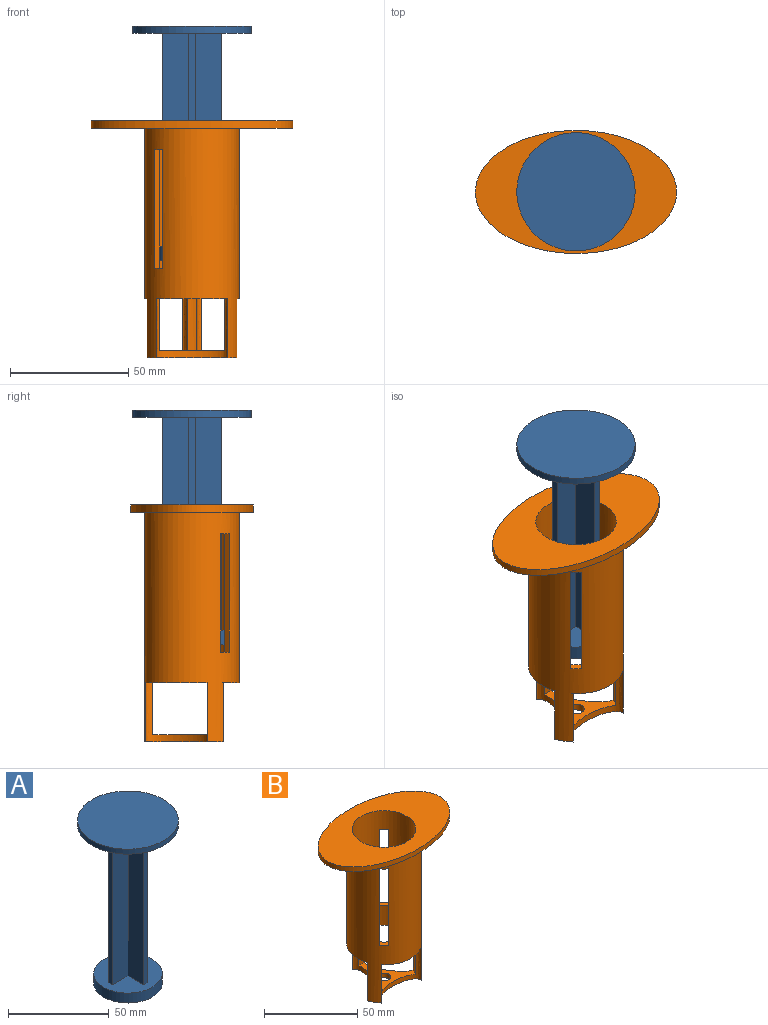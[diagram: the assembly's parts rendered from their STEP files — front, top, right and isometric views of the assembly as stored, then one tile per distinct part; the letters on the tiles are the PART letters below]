
ASSEMBLY  parts=2 mates=1
PART A: 18 faces, bbox 50x50x99 mm
  f0: plane 90x3mm, normal (0,1,0), area 270mm2, adj f1,f11,f12,f16
  f1: plane 90x11mm, normal (-1,0,0), area 990mm2, adj f0,f2,f12,f16
  f2: plane 90x11mm, normal (0,1,0), area 990mm2, adj f1,f3,f12,f16
  f3: plane 90x3mm, normal (-1,0,0), area 270mm2, adj f2,f4,f12,f16
  f4: plane 90x11mm, normal (0,-1,0), area 990mm2, adj f3,f5,f12,f16
  f5: plane 90x11mm, normal (-1,0,0), area 990mm2, adj f4,f6,f12,f16
  f6: plane 90x3mm, normal (0,-1,0), area 270mm2, adj f5,f7,f12,f16
  f7: plane 90x11mm, normal (1,0,0), area 990mm2, adj f6,f8,f12,f16
  f8: plane 90x11mm, normal (0,-1,0), area 990mm2, adj f7,f9,f12,f16
  f9: plane 90x3mm, normal (1,0,0), area 270mm2, adj f8,f10,f12,f16
  f10: plane 90x11mm, normal (0,1,0), area 990mm2, adj f9,f11,f12,f16
  f11: plane 90x11mm, normal (1,0,0), area 990mm2, adj f0,f10,f12,f16
  f12: plane 34x34mm, normal (0,0,1), area 766.9mm2, adj f0,f1,f2,f3,f4,f5,f6,f7
  f13: cylinder r=17mm len=34mm, axis (0,0,-1), area 640.9mm2, adj f12,f14
  f14: plane 34x34mm, normal (0,0,-1), area 907.9mm2, adj f13
  f15: cylinder r=25mm len=50mm, axis (0,0,1), area 471.2mm2, adj f16,f17
  f16: plane 50x50mm, normal (0,0,-1), area 1822.5mm2, adj f0,f1,f2,f3,f4,f5,f6,f7
  f17: plane 50x50mm, normal (0,0,1), area 1963.5mm2, adj f15
PART B: 22 faces, bbox 85x52x100 mm
  f0: cylinder r=20mm len=97mm, axis (0,0,-1), area 9146.2mm2, adj f2,f5,f6,f8,f9,f10,f11,f13
  f1: cylinder r=17mm len=97mm, axis (0,0,-1), area 7783.9mm2, adj f3,f4,f5,f6,f8,f9,f10,f11
  f2: plane 37.92x33.24mm, normal (0,0,-1), area 315.7mm2, adj f0,f5,f7,f8,f10
  f3: plane 85x52mm, normal (0,0,1), area 2563.5mm2, adj f1,f12
  f4: plane 31.3x27.23mm, normal (0,0,1), area 266.2mm2, adj f1,f5,f7,f8,f10
  f5: extruded ~29.98x25mm, area 258.3mm2, adj f0,f1,f2,f4,f6
  f6: plane 30x9.77mm, normal (0,0,-1), area 99.7mm2, adj f0,f1,f5
  f7: cylinder r=3.5mm len=7mm, axis (0,0,-1), area 66mm2, adj f2,f4
  f8: extruded ~26.49x25mm, area 258.3mm2, adj f0,f1,f2,f4,f9
  f9: plane 26.49x17.92mm, normal (0,0,-1), area 99.7mm2, adj f0,f1,f8
  f10: extruded ~26.49x25mm, area 258.3mm2, adj f0,f1,f2,f4,f11
  f11: plane 26.49x17.92mm, normal (0,0,-1), area 99.7mm2, adj f0,f1,f10
  f12: extruded ~85x52mm, area 655mm2, adj f3,f13
  f13: plane 85x52mm, normal (0,0,-1), area 2214.8mm2, adj f0,f12
  f14: plane 5.68x5.68mm, normal (0,0,1), area 15mm2, adj f0,f1,f15,f17
  f15: plane 50x2.14mm, normal (-0.71,0.71,0), area 151.4mm2, adj f0,f1,f14,f16
  f16: plane 5.68x5.68mm, normal (0,0,-1), area 15mm2, adj f0,f1,f15,f17
  f17: plane 50x2.14mm, normal (0.71,-0.71,0), area 151.4mm2, adj f0,f1,f14,f16
  f18: plane 50x2.14mm, normal (0.71,-0.71,0), area 151.4mm2, adj f0,f1,f19,f21
  f19: plane 5.68x5.68mm, normal (0,0,-1), area 15mm2, adj f0,f1,f18,f20
  f20: plane 50x2.14mm, normal (-0.71,0.71,0), area 151.4mm2, adj f0,f1,f19,f21
  f21: plane 5.68x5.68mm, normal (0,0,1), area 15mm2, adj f0,f1,f18,f20
PLACE A t=(0,0,-59)mm
PLACE B at identity
MATE slider A.f13 <-> B.f0  axis (0,0,-1) through (0,0,41)mm
